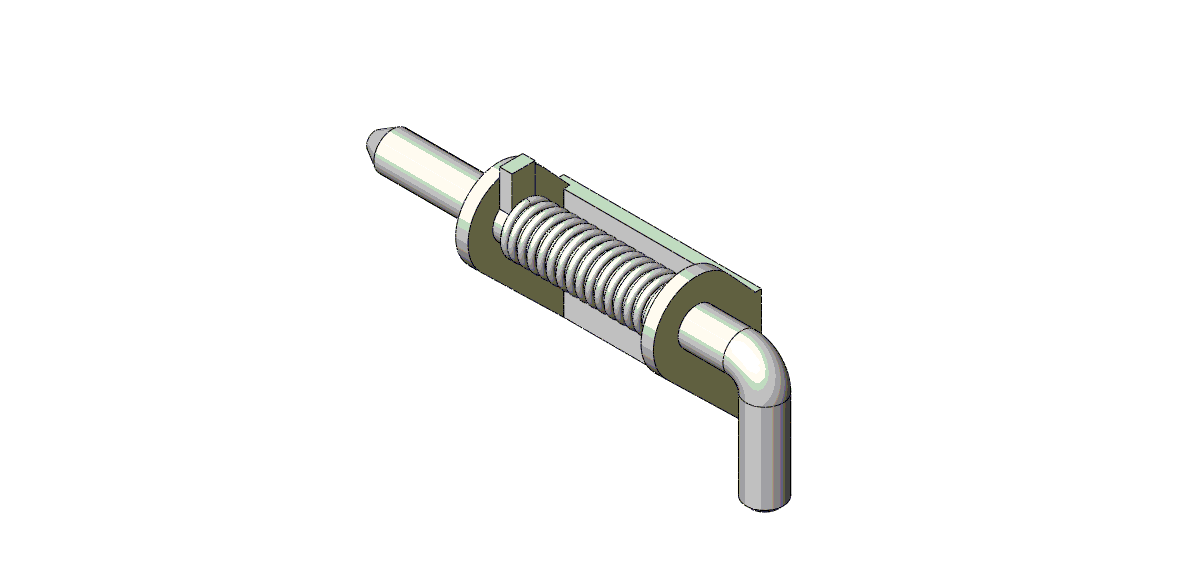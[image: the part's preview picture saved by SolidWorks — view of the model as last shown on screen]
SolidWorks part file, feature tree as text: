
SOLIDWORKS PART (.sldprt)
format: sldprt  version: not decoded by parser v0  size: 1,847,808 bytes
history: native  units: mm
features: sketch x12, plane x5, cut_extrude x3, extrude x2, sweep x2, chamfer x2, revolve x2, material x1, fillet x1, helix x1, mirror x1 (+13 scaffold rows collapsed)
feature tree (45):
  scaffold x13  (default folders/planes/origin — collapsed)
  material  "Plain Carbon Steel"
  sketch  "Sketch1"  dims[pin dia=9.525mm D4=10.795mm D1=~15.035446mm A=16.6624mm B=28.575mm wall thickness=3.175mm open width=39.6875mm]
  extrude  "Extrude1"  Depth=50.8mm bracket length=50.8mm
  plane  "Plane1"
  sketch  "Sketch2"  dims[D1=3.175mm D2=3.175mm]
  cut_extrude  "Cut-Extrude1"  [1 undecoded]
  sketch  "Sketch3"  dims[hole od=6.731mm screw center=28.575mm screw offset=9.525mm D4=2.54mm D1=11.1125mm]
  cut_extrude  "Cut-Extrude2"  [1 undecoded]
  fillet  "Fillet1"  Radius=2.3749mm
  plane  "Plane3"
  sketch  "Sketch6"  dims[D3=~5.953125mm pin extension=31.75mm Pin x=17.4625mm Pin Y=30.1752mm]
  plane  "Plane4"
  sketch  "Sketch7"  dims[D1=12.7mm]
  sweep  "Sweep1"
  chamfer  "Chamfer1"  Distance=2.54mm Angle=60deg
  chamfer  "Chamfer2"  Distance=1.27mm Angle=45deg
  sketch  "Sketch8"  dims[D1=~5.953125mm D2=~13.096875mm]
  extrude  "Extrude2"  Depth=3.175mm
  plane  "Plane5"  Offset=0.92075mm
  sketch  "Sketch9"  dims[D1=0.0mm]
  helix  "Helix/Spiral1"  Pitch=39.5605mm
  sketch  "Sketch15"  dims[D1=~0.79375mm D2=39.5605mm]
  sketch  "Sketch11"  dims[D1=1.5875mm]
  sweep  "Sweep3"
  sketch  "Sketch12"  dims[D1=0.0mm]
  revolve  "Revolve1"  Angle=235deg
  sketch  "Sketch13"  dims[D1=0.0mm]
  revolve  "Revolve2"  Angle=270deg
  sketch  "Sketch14"  dims[D1=~1.190625mm D2=0.9525mm]
  cut_extrude  "Cut-Extrude3"  Depth=76.2mm
  plane  "Plane6"  Offset=25.4mm
  mirror  "Mirror1"
decode coverage: 21 of 26 modeling features carry decoded parameters
note: ~ marks probable driven/reference dimensions
note: 2 parameter values undecoded
note: suppression state not decoded; provenance and decode notes live in map.json
